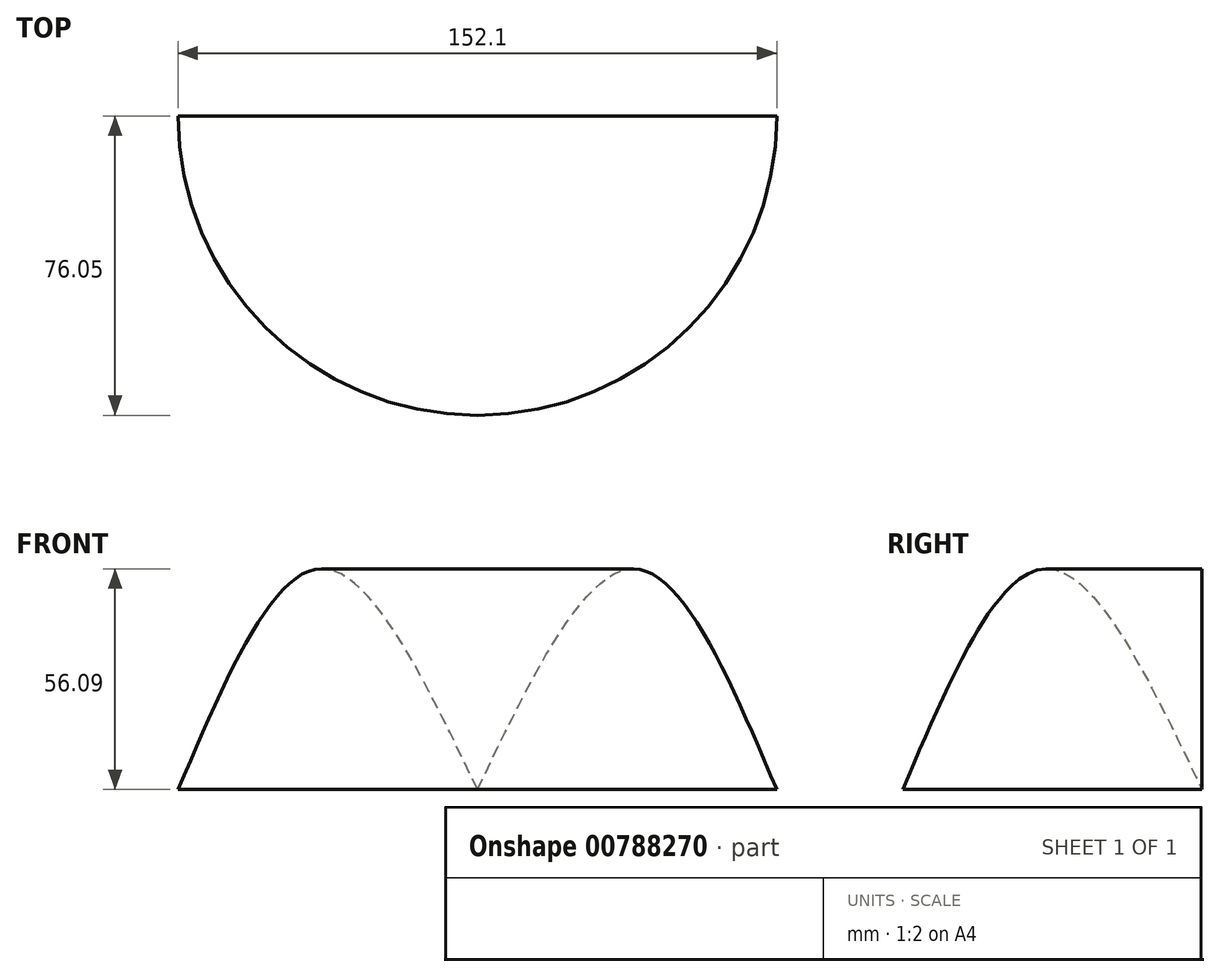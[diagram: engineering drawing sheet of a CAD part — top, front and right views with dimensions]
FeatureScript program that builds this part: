
annotation { "Feature Type Name" : "Feature", "Feature Type Description" : "" }
export const myFeature = defineFeature(function(context is Context, id is Id, definition is map)
    precondition{}
    {
        {
            var Q0;
            Q0=qCreatedBy(makeId("Front.planeOp"),FACE);
            var sketch = newSketch(context, id + "F0", { "sketchPlane" : qUnion([Q0])});
            skFitSpline(sketch, "E0", {"points": [v(0, 0) * mm, v(39.78, 56.08) * mm, v(76.05, 0) * mm], "startDerivative": vector(80.47, 167.85) * mm, "endDerivative": vector(71.6, -168.67) * mm});
            skLineSegment(sketch, "E1", {"start": v(0, 0) * mm, "end": v(76.05, 0) * mm});
            skSolve(sketch);
        }
        {
            var Q0;
            Q0=qCreatedBy(makeId("Front.planeOp"),FACE);
            var sketch = newSketch(context, id + "F1", { "sketchPlane" : qUnion([Q0])});
            skLineSegment(sketch, "E2", {"start": v(0, 75.16) * mm, "end": v(0, -75.57) * mm});
            skSolve(sketch);
        }
        {
            var Q0;
            Q0 = qSketchRegion(id + "F0", true);
            var Q1;
            Q1=sQuery(id+"F1.wireOp",EDGE,"E2");
            revolve(context, id + "F2", {"surfaceOperationType" : NewSurfaceOperationType.NEW, "entities" : qUnion([Q0]), "axis" : qUnion([Q1]), "revolveType" : RevolveType.ONE_DIRECTION, "angle" : 180 * degree});
        }
    });
